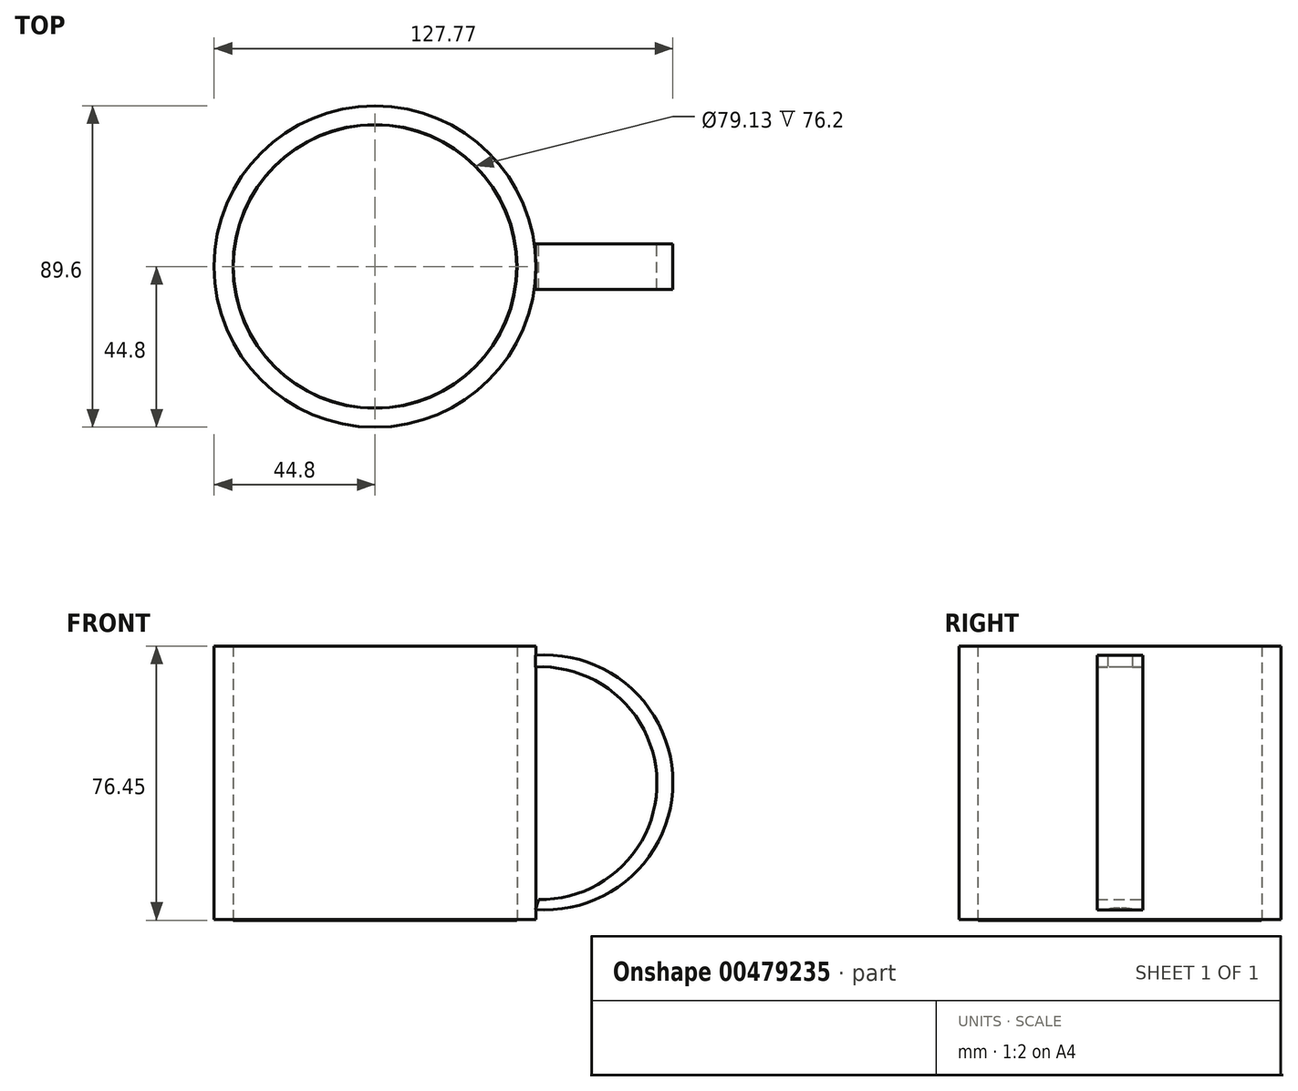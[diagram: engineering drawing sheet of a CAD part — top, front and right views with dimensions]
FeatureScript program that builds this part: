
annotation { "Feature Type Name" : "Feature", "Feature Type Description" : "" }
export const myFeature = defineFeature(function(context is Context, id is Id, definition is map)
    precondition{}
    {
        {
            var Q0;
            Q0=qCreatedBy(makeId("Top.planeOp"),FACE);
            var sketch = newSketch(context, id + "F0", { "sketchPlane" : qUnion([Q0])});
            skCircle(sketch, "E0", {"center": v(0, 0) * mm, "radius": 44.8 * mm});
            skCircle(sketch, "E1", {"center": v(0, 0) * mm, "radius": 39.56 * mm});
            skCircle(sketch, "E2", {"center": v(0, 0) * mm, "radius": 39.46 * mm});
            skSolve(sketch);
        }
        {
            var Q0;
            Q0=makeQuery(id+"F0.imprint","IMPRINT",FACE,{"disambiguationData":[TD([[makeQuery(id+"F0.imprint","IMPRINT",EDGE,{"derivedFrom":sQuery(id+"F0.wireOp",EDGE,"E0")}),1.0]])]});
            extrude(context, id + "F1", {"entities" : qUnion([Q0]), "depth" : 76.2 * mm});
        }
        {
            var Q0;
            Q0=makeQuery(id+"F0.imprint","IMPRINT",FACE,{"disambiguationData":[TD([[makeQuery(id+"F0.imprint","IMPRINT",EDGE,{"derivedFrom":sQuery(id+"F0.wireOp",EDGE,"E2")}),1.0]])]});
            extrude(context, id + "F2", {"entities" : qUnion([Q0]), "oppositeDirection" : true, "depth" : 0.25 * mm});
        }
        {
            var Q0;
            Q0=qCreatedBy(makeId("Front.planeOp"),FACE);
            var sketch = newSketch(context, id + "F3", { "sketchPlane" : qUnion([Q0])});
            skArc(sketch, "E3", {"start": v(45.53, 5.51) * mm, "mid": v(78.53, 38.37) * mm, "end": v(44.67, 70.35) * mm});
            skArc(sketch, "E4", {"start": v(44.67, 2.78) * mm, "mid": v(82.97, 38.17) * mm, "end": v(44.67, 73.57) * mm});
            skLineSegment(sketch, "E5", {"start": v(44.67, 70.35) * mm, "end": v(44.67, 73.57) * mm});
            skLineSegment(sketch, "E6", {"start": v(45.53, 5.51) * mm, "end": v(44.67, 2.78) * mm});
            skSolve(sketch);
        }
        {
            var Q0;
            Q0=makeQuery(id+"F3.imprint","IMPRINT",FACE,{"disambiguationData":[TD([[makeQuery(id+"F3.imprint","IMPRINT",EDGE,{"derivedFrom":sQuery(id+"F3.wireOp",EDGE,"E3")}),-1.0]])]});
            extrude(context, id + "F4", {"entities" : qUnion([Q0]), "operationType" : NewBodyOperationType.ADD, "depth" : 6.35 * mm, "hasSecondDirection" : true, "secondDirectionOppositeDirection" : true, "secondDirectionDepth" : 6.35 * mm});
        }
        {
            var Q0;
            Q0=qCreatedBy(makeId("Top.planeOp"),FACE);
            var sketch = newSketch(context, id + "F5", { "sketchPlane" : qUnion([Q0])});
            skLineSegment(sketch, "E7", {"start": v(-6.54, 43.16) * mm, "end": v(5.92, 43.16) * mm});
            skLineSegment(sketch, "E8", {"start": v(5.92, 43.16) * mm, "end": v(5.92, 50.03) * mm});
            skLineSegment(sketch, "E9", {"start": v(5.92, 50.03) * mm, "end": v(-6.54, 50.03) * mm});
            skLineSegment(sketch, "E10", {"start": v(-6.54, 50.03) * mm, "end": v(-6.54, 43.16) * mm});
            skSolve(sketch);
        }
        {
            var Q0;
            Q0=sQuery(id+"F5.wireOp",EDGE,"E9");
            var Q1;
            Q1=sQuery(id+"F5.wireOp",EDGE,"E8");
            var Q2;
            Q2=sQuery(id+"F5.wireOp",EDGE,"E10");
            var Q3;
            Q3=sQuery(id+"F5.wireOp",EDGE,"E7");
            extrude(context, id + "F6", {"bodyType" : ToolBodyType.SURFACE, "surfaceEntities" : qUnion([Q0, Q1, Q2, Q3]), "depth" : 71.37 * mm});
        }
    });
